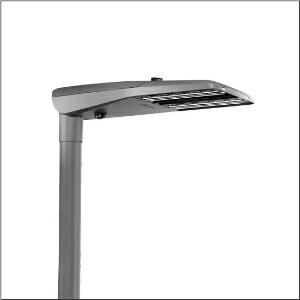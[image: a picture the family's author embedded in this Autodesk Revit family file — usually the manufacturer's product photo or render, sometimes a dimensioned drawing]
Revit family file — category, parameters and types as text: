
# Revit family: streetlight_sl_11_iq_midi___st1_0st0_5_5xc3j51y08me_1f9d
name_source: partatom
category: Lighting Fixtures
units: mm (PartAtom-declared; Revit-internal decimal feet)

## family parameters
Cut with Voids When Loaded = No
Host = Face
Light Source = No
Part Type = Normal
Room Calculation Point = No
Round Connector Dimension = Use Diameter
Shared = No

## types (1)
- --- (1 x LED, 17650 lm, 122.7 W, 3000K)
    Apparent Load = 123 VA
    CIE Flux Codes = 35 68 96 100 100
    Color Rendering = 70
    Color Temperature = 3000K
    Default Elevation = 1800 mm
    Description = Streetlight SL 11 iQ midi, mast luminaire, primary light control with 3 zone facetted reflector, of plastic, silver coated, highly specular, primary optical cover: cover, of PMMA, transparent, light distribution: ST1.0ST0.5, light emission: direct distribution, primary light characteristic: asymmetric, installation type: post-top, side-entry, LED, High Power LED, rated luminous flux: 17.650lm, luminous efficacy: 144lm/W, light colour: 730, colour temperature: 3000K, control: presetting dimming logarithmic, Street-Remote, Auto-Match, Temp-Guard, Lumen-Switch, Night-Set, Smart-Wire, Light-Fading, Desk-Remote (wireless, voltage-free reading and setting of iQ features in the workshop via application-optimized NFC function/RFID function), optimised constant luminous flux control (CLO 2.0), with cable H07RN-F 5x 1.5mm², mains connection: 230..240V, AC, 50/60Hz, connection cable pre-assembled, cable length: 12,5m, start of lifetime: 123W, end of service life: 130W, reduction: 56W, luminaire housing, of diecast aluminium, powder-coated, Siteco® metallic grey (DB 702S), please order mast flange separately, inclination adjustable without tools: 0°, 5°, 10°, 15° (post-top) | 0°, -5°, -10°, -15° (side-entry), sealing non-destructively replaceable, multi-level sealing system, length: 780mm, width: 376mm, height: 118mm, mast flange for spigot size: 42mm (side-entry): 5XC10008XM4, 60/48mm (side-entry/post-top): 5XC10108XM2, 76/60mm (side-entry/post-top): 5XC10108XM1, equipment: Power, Smart Interface below and above, protection rating (complete): IP66, insulation class (complete): insulation class II (safety insulation), certification: CE, ENEC, VDE, UKCA, impact resistance: IK09, permissible operating ambient temperature for outdoor applications: -25..+50°C, standard-compliant lighting for roads and squares, Environmental Product Declaration (EPD) tested and certified by an independent institute, packaging unit: 1 piece

Light Distribution: ST1.0ST0.5
    Height = 118 mm
    Lamp = 1 x LED
    Lamp Light Flux = 17650 lm
    Lamp Power = 122.7 W
    Lamp count = 1
    Length = 780 mm
    Luminous efficacy = 144 lm/W
    Manufacturer = Siteco
    ModVariant = No
    Model = 5XC3J51Y08ME
    Number of Poles = 1
    OnlyDefault = Yes
    Power Factor = 1
    Product Name = Streetlight SL 11 iQ midi | ST1.0ST0.5
    Product group = mast luminaire | pylon top
    ProductGroupID = 6100
    Protection Class = Protection class II
    Protection Degree = IP 66
    RLX_Detail_Level = 1
    RLX_Emergency_Light_Flux = 0 lm
    RLX_Emergency_Type = 0
    RLX_Emergency_Type_DB = No
    RlxData = <blob elided: 69745 chars, md5=d04cab08>
    Socket = socket
    Standby Power = 0 W
    System Light Flux = 17650 lm
    System Power = 123 W
    Type Comments = factory setting: luminous flux: 100 % | dim-lin: 254 | 553 mA
    Type Image = l_1004429.jpg
    URL = http://relux.com
    VarID = @adj_021761
    Voltage = 0 V
    Weight = 0.00 kg
    Width = 376 mm

## geometry (parser evidence)
native form markers: Blend x4, Sweep x8
no freeform markers — native parametric forms only
